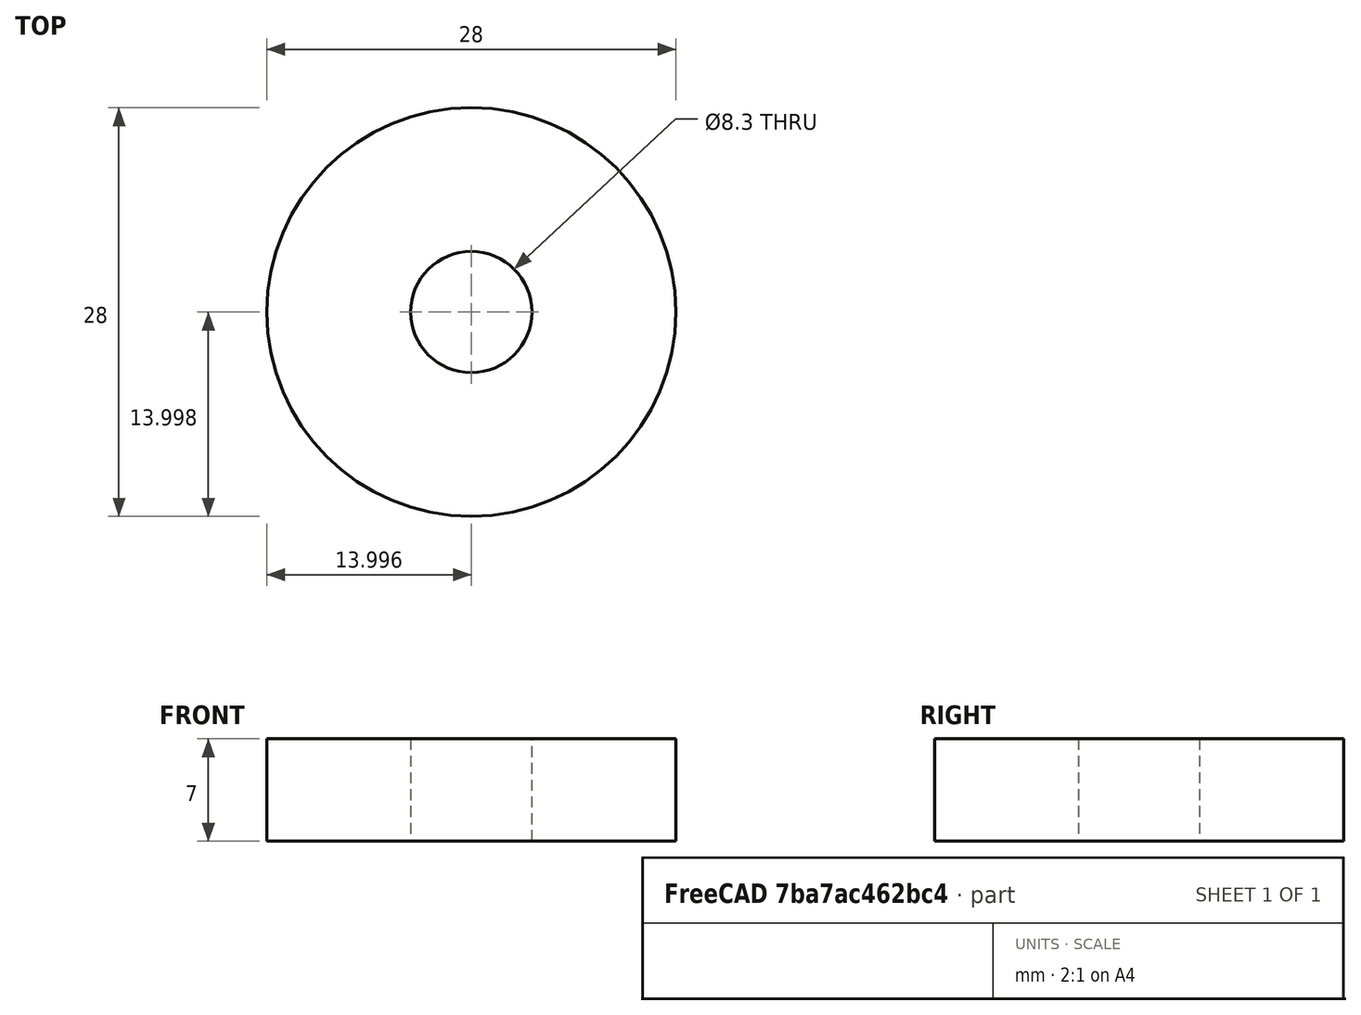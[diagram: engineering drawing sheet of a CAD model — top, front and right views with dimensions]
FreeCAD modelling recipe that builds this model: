
FCSTD DOCUMENT  (FreeCAD 0.21R33675 (Git))
Label: Brushless Cover
License: All rights reserved
LicenseURL: http://en.wikipedia.org/wiki/All_rights_reserved
objects: Sketcher::SketchObject×1, PartDesign::Pad×1, PartDesign::Body×1
note: 4 computed .brp shape members not serialized (recipe doc carries the construction recipe); baked Part::Feature solids carry a one-line shape summary decoded from their .brp

FEATURE [Sketcher::SketchObject] Sketch
  FullyConstrained = false
  MapMode = 5
  Support = -> [XY_Plane]
  sketch-geometry (2):
    g0: Circle CenterX=8.37571 CenterY=6.97849 CenterZ=0 NormalX=0 NormalY=0 NormalZ=1 AngleXU=0 Radius=14
    g1: Circle CenterX=8.37571 CenterY=6.97849 CenterZ=0 NormalX=0 NormalY=0 NormalZ=1 AngleXU=0 Radius=4.15
  constraints (3):
    c: Diameter(g0) = 28
    c: Coincident(g1,g0)
    c: Diameter(g1) = 8.3
FEATURE [PartDesign::Pad] Pad
  Direction = (0,0,1)
  Length = 7
  Length2 = 10
  Profile = -> Sketch
  ReferenceAxis = -> Sketch [N_Axis]
  Type = 0
FEATURE [PartDesign::Body] Body
  Group = -> [Sketch,Pad]
  Origin = -> Origin
  Tip = -> Pad
